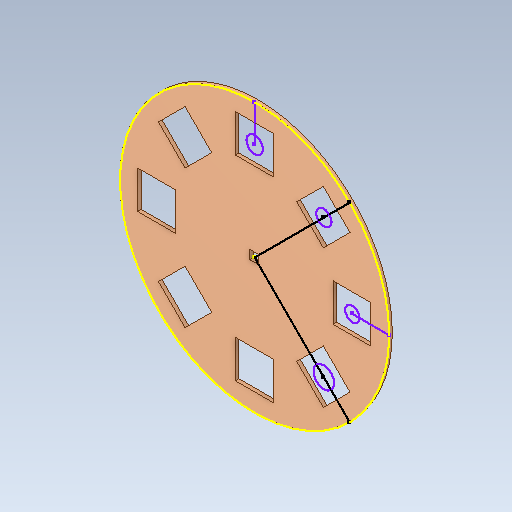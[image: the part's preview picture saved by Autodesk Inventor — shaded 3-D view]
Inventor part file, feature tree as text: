
AUTODESK INVENTOR PART (.ipt)
format: ipt  version: 2021 (Build 250183000, 183)  size: 143,872 bytes
history: native  units: mm
features: other x1, sketch x1
ambient origin geometry x8: Origin, YZ Plane, XZ Plane, XY Plane, X Axis, Y Axis, Z Axis, Center Point
bodies: Solid2 (feature_tree), Solid1 (feature_tree)
feature tree (2):
  other  "Repaired Geometry1"
  sketch  "Sketch3"
